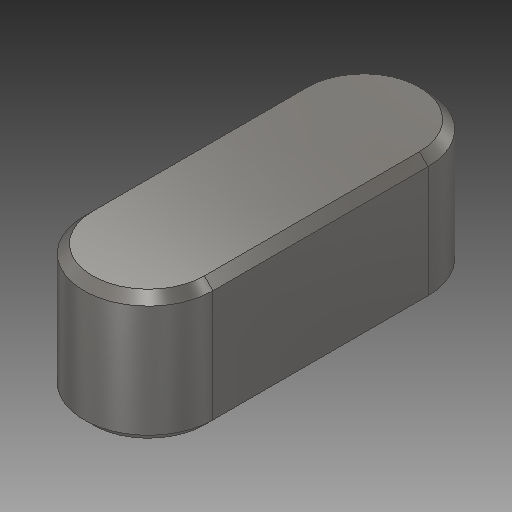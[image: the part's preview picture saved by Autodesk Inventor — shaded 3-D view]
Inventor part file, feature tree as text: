
AUTODESK INVENTOR PART (.ipt)
format: ipt  version: 2019.2 (Build 232265000, 265)  size: 124,416 bytes
history: native  units: mm
features: extrude x1, chamfer x1, sketch x1
ambient origin geometry x8: Origin, YZ Plane, XZ Plane, XY Plane, X Axis, Y Axis, Z Axis, Center Point
bodies: Solid1 (feature_tree)
feature tree (3):
  extrude  "Extrusion1"  Depth=3.0mm
  chamfer  "Chamfer1"  [1 undecoded]
  sketch  "Sketch1"  dims[d1=5.0mm d2=3.0mm d3=0.0mm d4=0.2mm d5=2.0mm d6=45.0deg d7=3.0mm]
note: 1 required parameter value undecoded (feature->parameter linkage not recoverable at this tier; creation-order binding heuristic only, values carry confidence <= 0.55)
